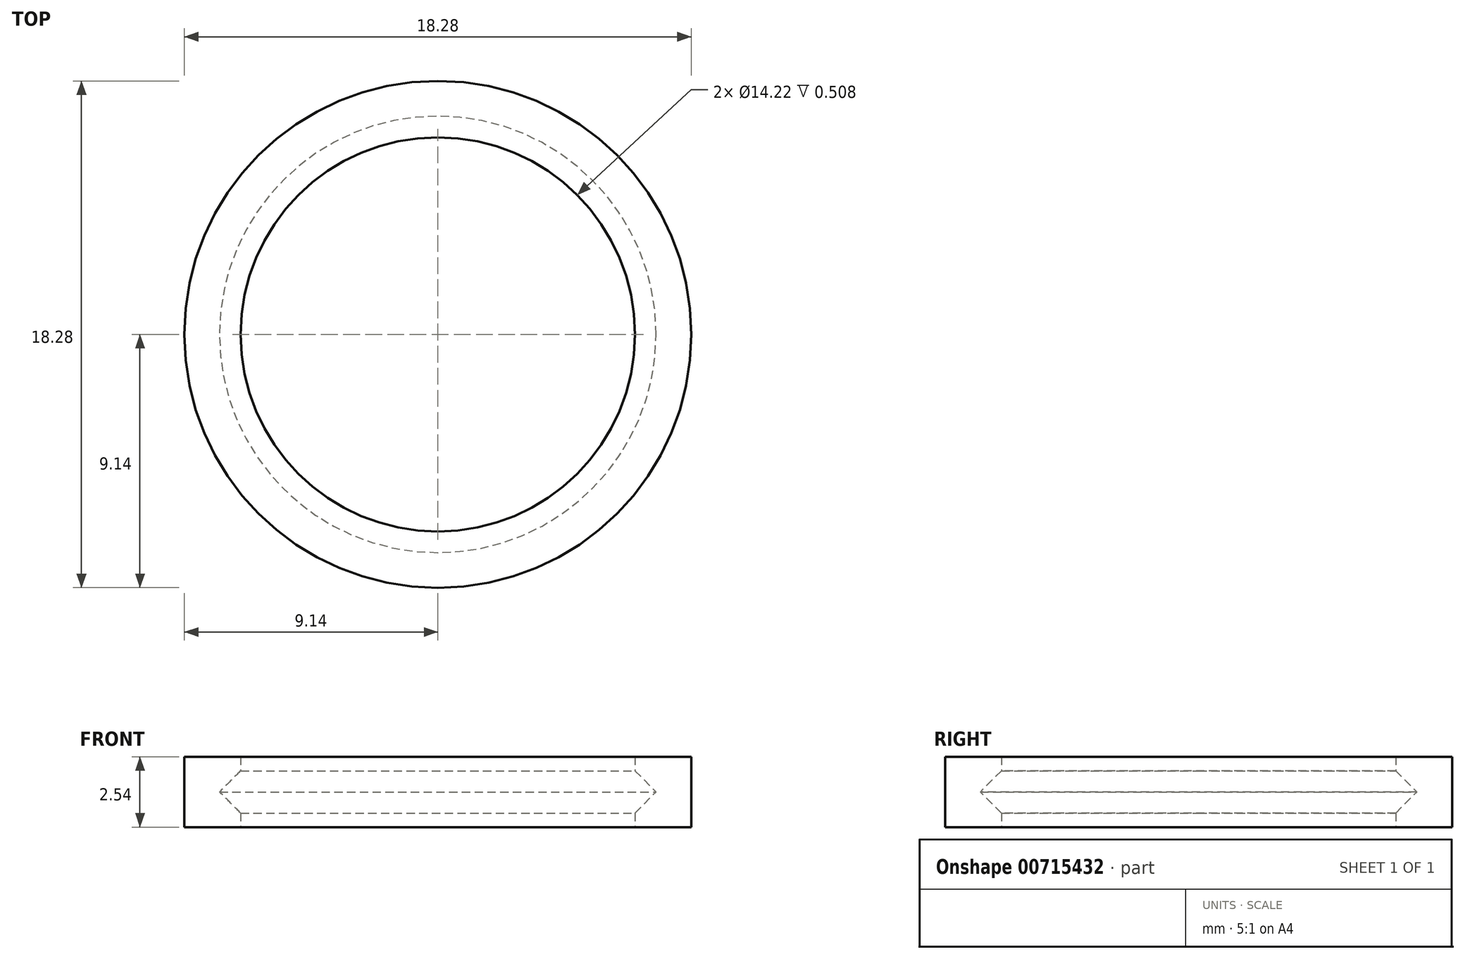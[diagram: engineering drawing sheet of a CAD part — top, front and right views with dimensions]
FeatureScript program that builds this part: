
annotation { "Feature Type Name" : "Feature", "Feature Type Description" : "" }
export const myFeature = defineFeature(function(context is Context, id is Id, definition is map)
    precondition{}
    {
        {
            var Q0;
            Q0=qCreatedBy(makeId("Front.planeOp"),FACE);
            var sketch = newSketch(context, id + "F0", { "sketchPlane" : qUnion([Q0])});
            skLineSegment(sketch, "E0", {"start": v(9.14, 0) * mm, "end": v(9.14, 2.54) * mm});
            skLineSegment(sketch, "E1", {"start": v(9.14, 2.54) * mm, "end": v(7.11, 2.54) * mm});
            skLineSegment(sketch, "E2", {"start": v(7.11, 2.54) * mm, "end": v(7.11, 2.03) * mm});
            skLineSegment(sketch, "E3", {"start": v(7.11, 2.03) * mm, "end": v(7.87, 1.27) * mm});
            skLineSegment(sketch, "E4", {"start": v(7.87, 1.27) * mm, "end": v(7.11, 0.5) * mm});
            skLineSegment(sketch, "E5", {"start": v(7.11, 0.5) * mm, "end": v(7.11, 0) * mm});
            skLineSegment(sketch, "E6", {"start": v(7.11, 0) * mm, "end": v(9.14, 0) * mm});
            skLineSegment(sketch, "E7", {"start": v(0, 0) * mm, "end": v(0, 1.78) * mm});
            skSolve(sketch);
        }
        {
            var Q0;
            Q0=makeQuery(id+"F0.imprint","IMPRINT",FACE,{"disambiguationData":[TD([[makeQuery(id+"F0.imprint","IMPRINT",EDGE,{"derivedFrom":sQuery(id+"F0.wireOp",EDGE,"E0")}),1.0]])]});
            var Q1;
            Q1=sQuery(id+"F0.wireOp",EDGE,"E7");
            revolve(context, id + "F1", {"surfaceOperationType" : NewSurfaceOperationType.NEW, "entities" : qUnion([Q0]), "axis" : qUnion([Q1]), "revolveType" : RevolveType.FULL});
        }
    });
